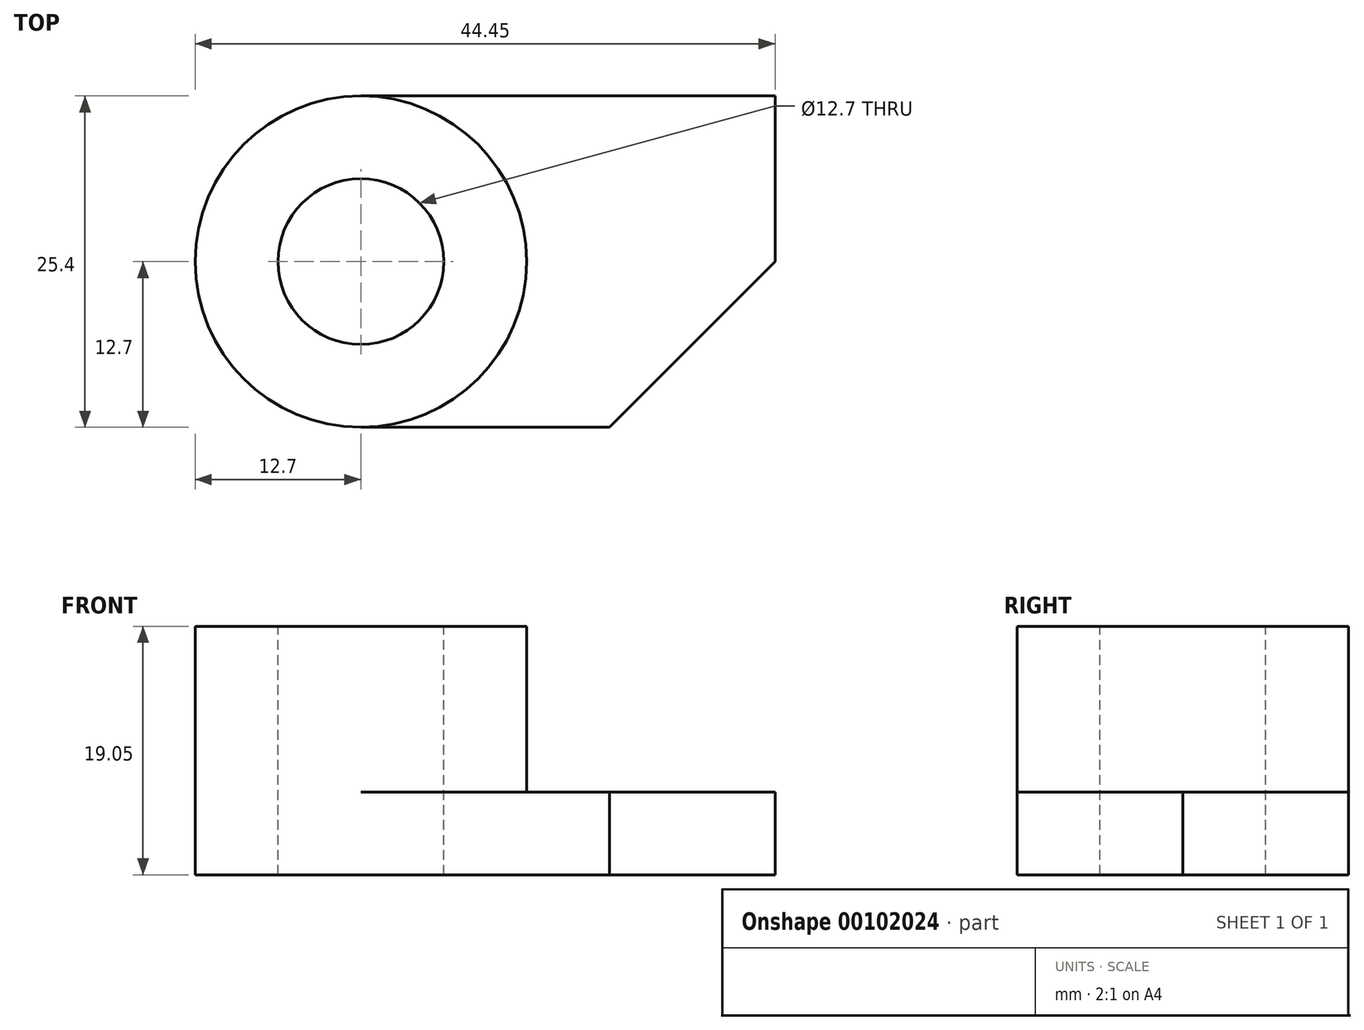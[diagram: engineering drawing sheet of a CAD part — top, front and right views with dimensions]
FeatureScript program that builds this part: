
annotation { "Feature Type Name" : "Feature", "Feature Type Description" : "" }
export const myFeature = defineFeature(function(context is Context, id is Id, definition is map)
    precondition{}
    {
        {
            var Q0;
            Q0=qCreatedBy(makeId("Top.planeOp"),FACE);
            var sketch = newSketch(context, id + "F0", { "sketchPlane" : qUnion([Q0])});
            skLineSegment(sketch, "E0", {"start": v(0, 0) * mm, "end": v(31.75, 0) * mm});
            skLineSegment(sketch, "E1", {"start": v(31.75, 0) * mm, "end": v(31.75, 25.4) * mm});
            skLineSegment(sketch, "E2", {"start": v(31.75, 25.4) * mm, "end": v(0, 25.4) * mm});
            skLineSegment(sketch, "E3", {"start": v(0, 25.4) * mm, "end": v(0, 0) * mm});
            skSolve(sketch);
        }
        {
            var Q0;
            Q0 = qSketchRegion(id + "F0", true);
            extrude(context, id + "F1", {"entities" : qUnion([Q0]), "depth" : 6.35 * mm});
        }
        {
            var Q0;
            Q0=makeQuery(id+"F1.opExtrude","CAP_FACE",FACE,{"disambiguationData":[OSD([sQuery(id+"F0.wireOp",EDGE,"E0"),sQuery(id+"F0.wireOp",EDGE,"E1"),sQuery(id+"F0.wireOp",EDGE,"E2"),sQuery(id+"F0.wireOp",EDGE,"E3")])],"isStart":true});
            var sketch = newSketch(context, id + "F2", { "sketchPlane" : qUnion([Q0])});
            skCircle(sketch, "E4", {"center": v(0, -12.7) * mm, "radius": 12.7 * mm});
            skSolve(sketch);
        }
        {
            var Q0;
            Q0 = qSketchRegion(id + "F2", true);
            extrude(context, id + "F3", {"entities" : qUnion([Q0]), "operationType" : NewBodyOperationType.ADD, "oppositeDirection" : true, "depth" : 19.05 * mm});
        }
        {
            var Q0;
            Q0=makeQuery(id+"F3.opExtrude","CAP_FACE",FACE,{"disambiguationData":[OSD([sQuery(id+"F2.wireOp",EDGE,"E4")])],"isStart":false});
            var sketch = newSketch(context, id + "F4", { "sketchPlane" : qUnion([Q0])});
            skCircle(sketch, "E5", {"center": v(0, 12.7) * mm, "radius": 6.35 * mm});
            skSolve(sketch);
        }
        {
            var Q0;
            Q0=makeQuery(id+"F4.imprint","IMPRINT",FACE,{"disambiguationData":[TD([[makeQuery(id+"F4.imprint","IMPRINT",EDGE,{"derivedFrom":sQuery(id+"F4.wireOp",EDGE,"E5")}),1.0]])]});
            extrude(context, id + "F5", {"entities" : qUnion([Q0]), "operationType" : NewBodyOperationType.REMOVE, "oppositeDirection" : true, "depth" : 25.4 * mm});
        }
        {
            var Q0;
            Q0=makeQuery(id+"F1.opExtrude","CAP_FACE",FACE,{"disambiguationData":[OSD([sQuery(id+"F0.wireOp",EDGE,"E0"),sQuery(id+"F0.wireOp",EDGE,"E1"),sQuery(id+"F0.wireOp",EDGE,"E2"),sQuery(id+"F0.wireOp",EDGE,"E3")])],"isStart":false});
            var sketch = newSketch(context, id + "F6", { "sketchPlane" : qUnion([Q0])});
            skLineSegment(sketch, "E6", {"start": v(31.75, 0) * mm, "end": v(31.75, 12.7) * mm});
            skLineSegment(sketch, "E7", {"start": v(19.05, 0) * mm, "end": v(31.75, 0) * mm});
            skLineSegment(sketch, "E8", {"start": v(31.75, 12.7) * mm, "end": v(19.05, 0) * mm});
            skSolve(sketch);
        }
        {
            var Q0;
            Q0=makeQuery(id+"F6.imprint","IMPRINT",FACE,{"disambiguationData":[TD([[makeQuery(id+"F6.imprint","IMPRINT",EDGE,{"derivedFrom":sQuery(id+"F6.wireOp",EDGE,"E6")}),1.0]])]});
            extrude(context, id + "F7", {"entities" : qUnion([Q0]), "operationType" : NewBodyOperationType.REMOVE, "oppositeDirection" : true, "depth" : 25.4 * mm});
        }
    });
